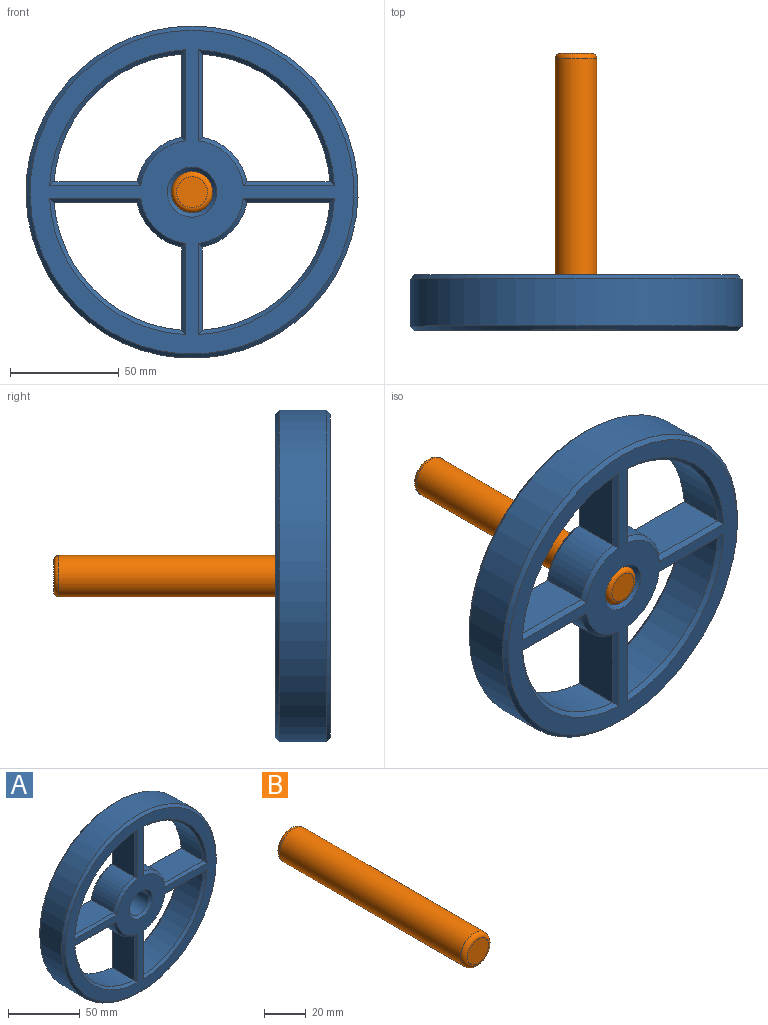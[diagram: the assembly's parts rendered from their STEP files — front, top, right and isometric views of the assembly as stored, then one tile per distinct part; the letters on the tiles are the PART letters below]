
ASSEMBLY  parts=2 mates=1
PART A: 56 faces, bbox 152.4x25.4x152.4 mm
  f0: cylinder r=25.61mm len=21.59mm, axis (0,1,0), area 661.6mm2, adj f1,f12,f31,f49
  f1: plane 38.16x21.59mm, normal (0,0,1), area 823.9mm2, adj f0,f2,f30,f48
  f2: cylinder r=63.5mm len=58.56mm, axis (0,1,0), area 1947.7mm2, adj f1,f12,f28,f46
  f3: cylinder r=25.61mm len=21.59mm, axis (0,1,0), area 661.6mm2, adj f4,f13,f23,f41
  f4: plane 38.16x21.59mm, normal (0,0,-1), area 823.9mm2, adj f3,f5,f22,f40
  f5: cylinder r=63.5mm len=58.56mm, axis (0,1,0), area 1947.7mm2, adj f4,f13,f20,f38
  f6: cylinder r=25.61mm len=21.59mm, axis (0,1,0), area 661.6mm2, adj f7,f14,f36,f54
  f7: plane 38.16x21.59mm, normal (-1,0,0), area 823.9mm2, adj f6,f8,f35,f53
  f8: cylinder r=63.5mm len=58.56mm, axis (0,1,0), area 1947.7mm2, adj f7,f14,f33,f51
  f9: plane 38.16x21.59mm, normal (0,0,1), area 823.9mm2, adj f10,f16,f25,f43
  f10: cylinder r=25.61mm len=21.59mm, axis (0,1,0), area 661.6mm2, adj f9,f11,f27,f45
  f11: plane 38.16x21.59mm, normal (1,0,0), area 823.9mm2, adj f10,f16,f26,f44
  f12: plane 38.16x21.59mm, normal (-1,0,0), area 823.9mm2, adj f0,f2,f29,f47
  f13: plane 38.16x21.59mm, normal (1,0,0), area 823.9mm2, adj f3,f5,f21,f39
  f14: plane 38.16x21.59mm, normal (0,0,-1), area 823.9mm2, adj f6,f8,f34,f52
  f15: cylinder r=9.53mm len=21.59mm, axis (0,1,0), area 1292.1mm2, adj f32,f50
  f16: cylinder r=63.5mm len=58.56mm, axis (0,1,0), area 1947.7mm2, adj f9,f11,f24,f42
  f17: cylinder r=76.2mm len=152.4mm, axis (0,1,0), area 10336.8mm2, adj f37,f55
  f18: plane 148.59x148.59mm, normal (0,-1,0), area 6210.4mm2, adj f20,f21,f22,f23,f24,f25,f26,f27
  f19: plane 148.59x148.59mm, normal (0,1,0), area 6210.4mm2, adj f38,f39,f40,f41,f42,f43,f44,f45
  f20: cone r=63.5mm half-angle=45deg, axis (0,-1,0), area 252.2mm2, adj f5,f18,f21,f22
  f21: plane 41.81x1.91mm, normal (0.71,-0.71,0), area 107.7mm2, adj f13,f18,f20,f23
  f22: plane 41.81x1.91mm, normal (0,-0.71,-0.71), area 107.7mm2, adj f4,f18,f20,f23
  f23: cone r=23.7mm half-angle=45deg, axis (0,1,0), area 83.7mm2, adj f3,f18,f21,f22
  f24: cone r=63.5mm half-angle=45deg, axis (0,-1,0), area 252.2mm2, adj f16,f18,f25,f26
  f25: plane 41.81x1.91mm, normal (0,-0.71,0.71), area 107.7mm2, adj f9,f18,f24,f27
  f26: plane 41.81x1.91mm, normal (0.71,-0.71,0), area 107.7mm2, adj f11,f18,f24,f27
  f27: cone r=23.7mm half-angle=45deg, axis (0,1,0), area 83.7mm2, adj f10,f18,f25,f26
  f28: cone r=63.5mm half-angle=45deg, axis (0,-1,0), area 252.2mm2, adj f2,f18,f29,f30
  f29: plane 41.81x1.91mm, normal (-0.71,-0.71,0), area 107.7mm2, adj f12,f18,f28,f31
  f30: plane 41.81x1.91mm, normal (0,-0.71,0.71), area 107.7mm2, adj f1,f18,f28,f31
  f31: cone r=23.7mm half-angle=45deg, axis (0,1,0), area 83.7mm2, adj f0,f18,f29,f30
  f32: cone r=9.53mm half-angle=45deg, axis (0,-1,0), area 177.4mm2, adj f15,f18
  f33: cone r=63.5mm half-angle=45deg, axis (0,-1,0), area 252.2mm2, adj f8,f18,f34,f35
  f34: plane 41.81x1.91mm, normal (0,-0.71,-0.71), area 107.7mm2, adj f14,f18,f33,f36
  f35: plane 41.81x1.91mm, normal (-0.71,-0.71,0), area 107.7mm2, adj f7,f18,f33,f36
  f36: cone r=23.7mm half-angle=45deg, axis (0,1,0), area 83.7mm2, adj f6,f18,f34,f35
  f37: cone r=74.3mm half-angle=45deg, axis (0,1,0), area 1273.7mm2, adj f17,f18
  f38: cone r=65.41mm half-angle=45deg, axis (0,1,0), area 252.2mm2, adj f5,f19,f39,f40
  f39: plane 41.81x1.91mm, normal (0.71,0.71,0), area 107.7mm2, adj f13,f19,f38,f41
  f40: plane 41.81x1.91mm, normal (0,0.71,-0.71), area 107.7mm2, adj f4,f19,f38,f41
  f41: cone r=25.61mm half-angle=45deg, axis (0,-1,0), area 83.7mm2, adj f3,f19,f39,f40
  f42: cone r=65.41mm half-angle=45deg, axis (0,1,0), area 252.2mm2, adj f16,f19,f43,f44
  f43: plane 41.81x1.91mm, normal (0,0.71,0.71), area 107.7mm2, adj f9,f19,f42,f45
  f44: plane 41.81x1.91mm, normal (0.71,0.71,0), area 107.7mm2, adj f11,f19,f42,f45
  f45: cone r=25.61mm half-angle=45deg, axis (0,-1,0), area 83.7mm2, adj f10,f19,f43,f44
  f46: cone r=65.41mm half-angle=45deg, axis (0,1,0), area 252.2mm2, adj f2,f19,f47,f48
  f47: plane 41.81x1.91mm, normal (-0.71,0.71,0), area 107.7mm2, adj f12,f19,f46,f49
  f48: plane 41.81x1.91mm, normal (0,0.71,0.71), area 107.7mm2, adj f1,f19,f46,f49
  f49: cone r=25.61mm half-angle=45deg, axis (0,-1,0), area 83.7mm2, adj f0,f19,f47,f48
  f50: cone r=11.43mm half-angle=45deg, axis (0,1,0), area 177.4mm2, adj f15,f19
  f51: cone r=65.41mm half-angle=45deg, axis (0,1,0), area 252.2mm2, adj f8,f19,f52,f53
  f52: plane 41.81x1.91mm, normal (0,0.71,-0.71), area 107.7mm2, adj f14,f19,f51,f54
  f53: plane 41.81x1.91mm, normal (-0.71,0.71,0), area 107.7mm2, adj f7,f19,f51,f54
  f54: cone r=25.61mm half-angle=45deg, axis (0,-1,0), area 83.7mm2, adj f6,f19,f52,f53
  f55: cone r=76.2mm half-angle=45deg, axis (0,-1,0), area 1273.7mm2, adj f17,f19
PART B: 5 faces, bbox 20.6x127x20.6 mm
  f0: cylinder r=9.53mm len=122.17mm, axis (0,1,0), area 7311.8mm2, adj f3,f4
  f1: plane 14.22x14.22mm, normal (0,-1,0), area 158.9mm2, adj f3
  f2: plane 14.22x14.22mm, normal (0,1,0), area 158.9mm2, adj f4
  f3: torus R=7.11mm, axis (0,-1,0), area 206mm2, adj f0,f1
  f4: torus R=7.11mm, axis (0,-1,0), area 206mm2, adj f0,f2
PLACE A rot(axis=(1,0,0),180deg) t=(-31.91,32.85,33.42)mm
PLACE B rot(axis=(1,0,0),180deg) t=(-31.91,83.65,33.42)mm
MATE cylindrical A.f0 <-> B.f0  axis (0,-1,0) through (-31.91,20.15,33.42)mm
